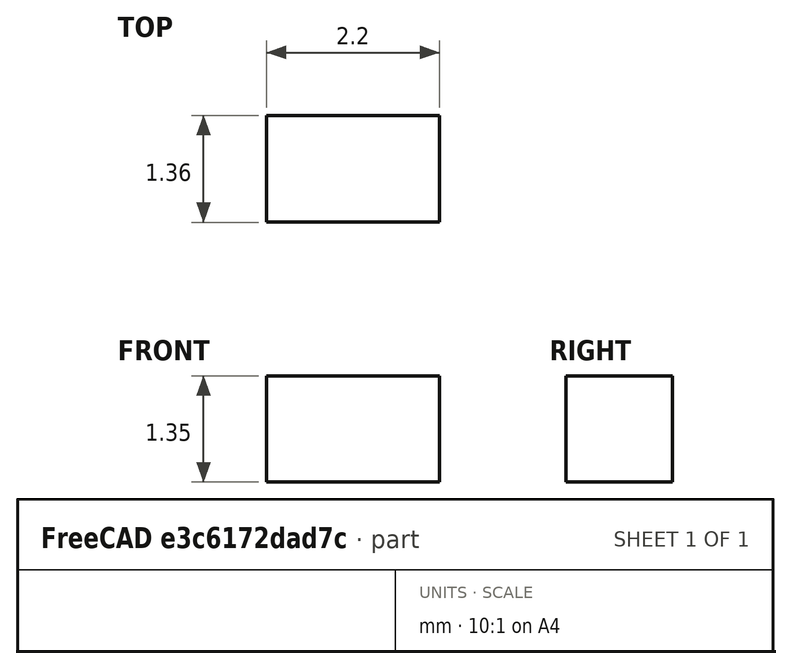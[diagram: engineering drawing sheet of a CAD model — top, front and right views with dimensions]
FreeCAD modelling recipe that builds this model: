
FCSTD DOCUMENT  (FreeCAD 0.18R15969 (Git))
Label: Capacitor 1u
License: All rights reserved
LicenseURL: http://en.wikipedia.org/wiki/All_rights_reserved
objects: Sketcher::SketchObject×1, PartDesign::Pad×1, PartDesign::Body×1
note: 4 computed .brp shape members not serialized (recipe doc carries the construction recipe); baked Part::Feature solids carry a one-line shape summary decoded from their .brp

FEATURE [Sketcher::SketchObject] Sketch
  MapMode = 5
  Support = -> [XY_Plane]
  expr: Constraints[16] = 2.1 + 0.1
  expr: Constraints[17] = 1.25 + 0.1
  sketch-geometry (7):
    g0: LineSegment StartX=-1.1 StartY=-0.675 StartZ=0 EndX=1.1 EndY=-0.675 EndZ=0
    g1: LineSegment StartX=1.1 StartY=-0.675 StartZ=0 EndX=1.1 EndY=0.675 EndZ=0
    g2: LineSegment StartX=1.1 StartY=0.675 StartZ=0 EndX=-1.1 EndY=0.675 EndZ=0
    g3: LineSegment StartX=-1.1 StartY=0.675 StartZ=0 EndX=-1.1 EndY=-0.675 EndZ=0
    g4: LineSegment [constr] StartX=-1.1 StartY=0.675 StartZ=0 EndX=0 EndY=-1e-16 EndZ=0
    g5: LineSegment [constr] StartX=0 StartY=0 StartZ=0 EndX=1.1 EndY=0.675 EndZ=0
    g6: LineSegment [constr] StartX=0 StartY=0 StartZ=0 EndX=-1.1 EndY=-0.675 EndZ=0
  constraints (18):
    c: Coincident(g0,g1)
    c: Coincident(g1,g2)
    c: Coincident(g2,g3)
    c: Coincident(g3,g0)
    c: Horizontal(g0)
    c: Horizontal(g2)
    c: Vertical(g1)
    c: Vertical(g3)
    c: Coincident(g4,g2)
    c: Coincident(g4,g-1)
    c: Coincident(g5,g-1)
    c: Coincident(g5,g1)
    c: Coincident(g6,g-1)
    c: Coincident(g6,g0)
    c: Equal(g5,g4)
    c: Equal(g4,g6)
    c: DistanceX(g2,g2) = 2.2
    c: DistanceY(g3,g3) = 1.35
FEATURE [PartDesign::Pad] Pad
  Length = 1.35
  Length2 = 100
  Profile = -> Sketch
  Refine = true
  Type = 0
  expr: Length = 1.25 + 0.1
FEATURE [PartDesign::Body] Body  label="Capacitor 1u"
  Group = -> [Sketch,Pad]
  Origin = -> Origin
  Tip = -> Pad
